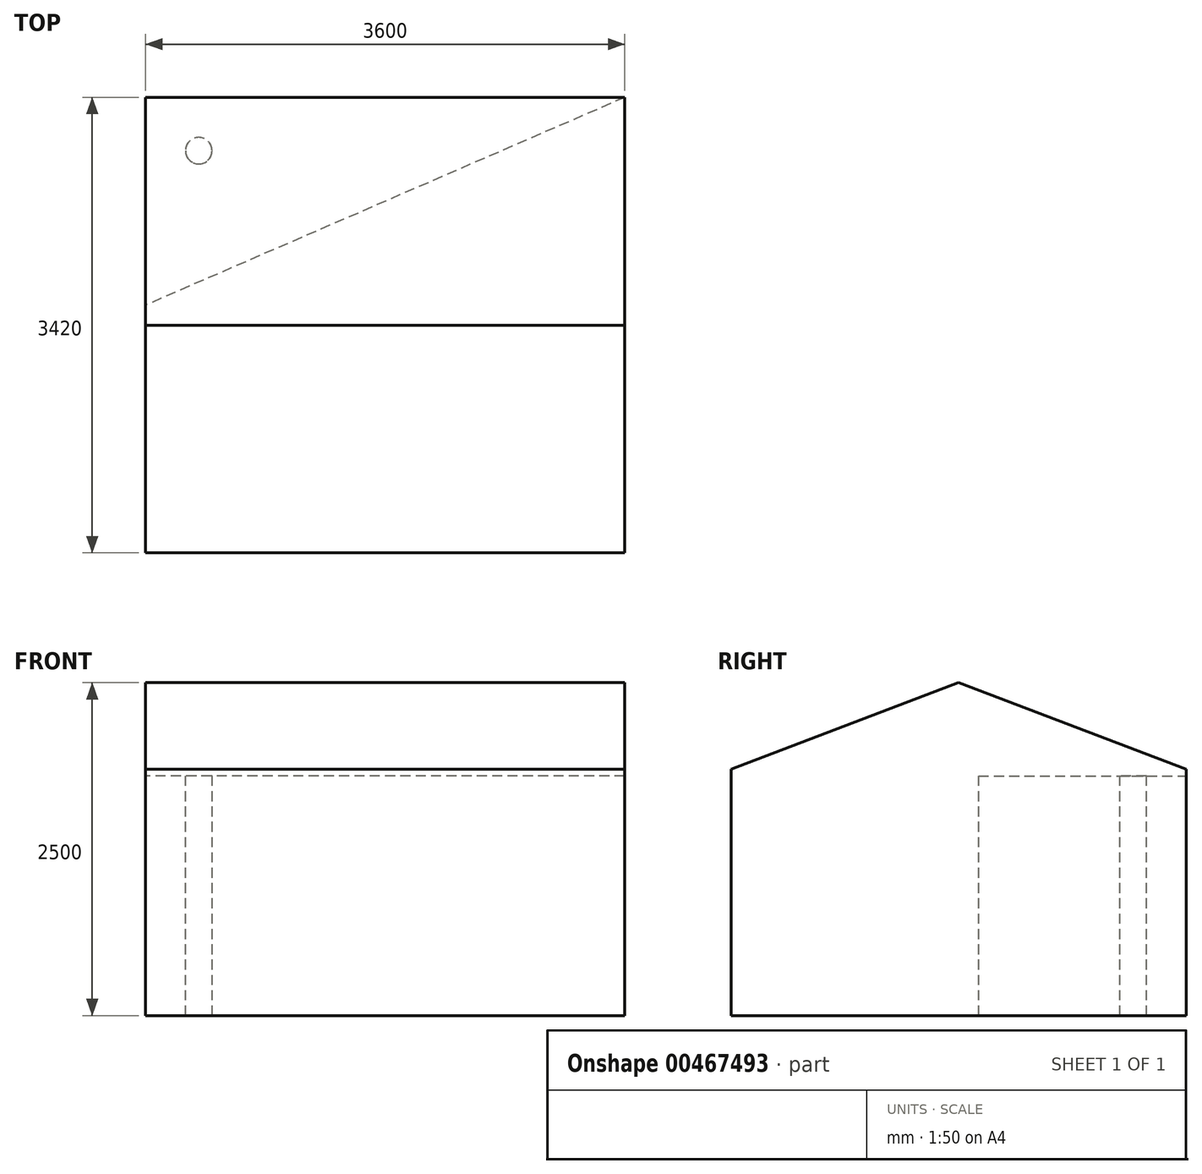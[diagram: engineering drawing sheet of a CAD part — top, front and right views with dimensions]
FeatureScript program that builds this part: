
annotation { "Feature Type Name" : "Feature", "Feature Type Description" : "" }
export const myFeature = defineFeature(function(context is Context, id is Id, definition is map)
    precondition{}
    {
        {
            var Q0;
            Q0=qCreatedBy(makeId("Top.planeOp"),FACE);
            var sketch = newSketch(context, id + "F0", { "sketchPlane" : qUnion([Q0])});
            skLineSegment(sketch, "E0.bottom", {"start": v(-1800, -1710) * mm, "end": v(1800, -1710) * mm});
            skLineSegment(sketch, "E0.left", {"start": v(-1800, -1710) * mm, "end": v(-1800, 150) * mm});
            skLineSegment(sketch, "E0.right", {"start": v(1800, -1710) * mm, "end": v(1800, 150) * mm});
            skPoint(sketch, "E0.middle", {"position": v(0, 0) * mm});
            skPoint(sketch, "E0.top.end.orphan", {"position": v(1800, 1710) * mm});
            skLineSegment(sketch, "E1.right", {"start": v(1800, 1710) * mm, "end": v(1800, 150) * mm});
            skLineSegment(sketch, "E2", {"start": v(1800, 1710) * mm, "end": v(-1800, 150) * mm});
            skPoint(sketch, "E3.orphan", {"position": v(-1800, 1710) * mm});
            skSolve(sketch);
        }
        {
            var Q0;
            Q0=makeQuery(id+"F0.imprint","IMPRINT",FACE,{"disambiguationData":[TD([[makeQuery(id+"F0.imprint","IMPRINT",EDGE,{"derivedFrom":sQuery(id+"F0.wireOp",EDGE,"E0.bottom")}),1.0]])]});
            extrude(context, id + "F1", {"entities" : qUnion([Q0]), "oppositeDirection" : true, "depth" : 1800 * mm});
        }
        {
            var Q0;
            Q0=makeQuery(id+"F1.opExtrude","CAP_FACE",FACE,{"disambiguationData":[OSD([sQuery(id+"F0.wireOp",EDGE,"E0.bottom"),sQuery(id+"F0.wireOp",EDGE,"E0.left"),sQuery(id+"F0.wireOp",EDGE,"E0.right"),sQuery(id+"F0.wireOp",EDGE,"E1.right"),sQuery(id+"F0.wireOp",EDGE,"E2")])],"isStart":true});
            var sketch = newSketch(context, id + "F2", { "sketchPlane" : qUnion([Q0])});
            skLineSegment(sketch, "E4.bottom", {"start": v(-1800, -1710) * mm, "end": v(1800, -1710) * mm});
            skLineSegment(sketch, "E4.top", {"start": v(-1800, 1710) * mm, "end": v(1800, 1710) * mm});
            skLineSegment(sketch, "E4.left", {"start": v(-1800, -1710) * mm, "end": v(-1800, 1710) * mm});
            skLineSegment(sketch, "E4.right", {"start": v(1800, -1710) * mm, "end": v(1800, 1710) * mm});
            skSolve(sketch);
        }
        {
            var Q0;
            Q0 = qSketchRegion(id + "F2", true);
            extrude(context, id + "F3", {"entities" : qUnion([Q0]), "operationType" : NewBodyOperationType.ADD, "depth" : 50 * mm});
        }
        {
            var Q0;
            Q0=makeQuery(id+"F3.boolean.opBoolean","MERGE",FACE,{"derivedFrom":[makeQuery(id+"F1.opExtrude","SWEPT_FACE",FACE,{"disambiguationData":[OSD([sQuery(id+"F0.wireOp",EDGE,"E0.right"),sQuery(id+"F0.wireOp",EDGE,"E1.right")])]}),makeQuery(id+"F3.opExtrude","SWEPT_FACE",FACE,{"disambiguationData":[OSD([sQuery(id+"F2.wireOp",EDGE,"E4.right")])]})]});
            var sketch = newSketch(context, id + "F4", { "sketchPlane" : qUnion([Q0])});
            skLineSegment(sketch, "E5", {"start": v(0, -1800) * mm, "end": v(0, 700) * mm});
            skPoint(sketch, "E5.endSnap0", {"position": v(0, -1800) * mm});
            skLineSegment(sketch, "E6", {"start": v(-1710, 50) * mm, "end": v(0, 700) * mm});
            skLineSegment(sketch, "E7", {"start": v(0, 700) * mm, "end": v(1710, 50) * mm});
            skSolve(sketch);
        }
        {
            var Q0;
            Q0=makeQuery(id+"F3.boolean.opBoolean","MERGE",FACE,{"derivedFrom":[makeQuery(id+"F1.opExtrude","SWEPT_FACE",FACE,{"disambiguationData":[OSD([sQuery(id+"F0.wireOp",EDGE,"E0.left")])]}),makeQuery(id+"F3.opExtrude","SWEPT_FACE",FACE,{"disambiguationData":[OSD([sQuery(id+"F2.wireOp",EDGE,"E4.left")])]})]});
            var sketch = newSketch(context, id + "F5", { "sketchPlane" : qUnion([Q0])});
            skLineSegment(sketch, "E8", {"start": v(0, -1800) * mm, "end": v(0, 700) * mm});
            skLineSegment(sketch, "E9", {"start": v(0, 700) * mm, "end": v(-1710, 50) * mm});
            skLineSegment(sketch, "E10", {"start": v(0, 700) * mm, "end": v(1710, 50) * mm});
            skSolve(sketch);
        }
        {
            var Q0;
            {var subQ0=sQuery(id+"F5.wireOp",EDGE,"E9");Q0=makeQuery(id+"F5.imprint","IMPRINT",FACE,{"disambiguationData":[TD([[makeQuery(id+"F5.imprint","IMPRINT",EDGE,{"derivedFrom":subQ0}),1.0]])]});}
            var Q1;
            {var subQ0=sQuery(id+"F5.wireOp",EDGE,"E10");Q1=makeQuery(id+"F5.imprint","IMPRINT",FACE,{"disambiguationData":[TD([[makeQuery(id+"F5.imprint","IMPRINT",EDGE,{"derivedFrom":subQ0}),-1.0]])]});}
            extrude(context, id + "F6", {"entities" : qUnion([Q0, Q1]), "operationType" : NewBodyOperationType.ADD, "oppositeDirection" : true, "depth" : 3600 * mm});
        }
        {
            var Q0;
            Q0=makeQuery(id+"F3.opExtrude","CAP_FACE",FACE,{"disambiguationData":[OSD([sQuery(id+"F2.wireOp",EDGE,"E4.bottom"),sQuery(id+"F2.wireOp",EDGE,"E4.top"),sQuery(id+"F2.wireOp",EDGE,"E4.left"),sQuery(id+"F2.wireOp",EDGE,"E4.right")])],"isStart":true});
            var sketch = newSketch(context, id + "F7", { "sketchPlane" : qUnion([Q0])});
            skLineSegment(sketch, "E11.bottom", {"start": v(-1800, -1710) * mm, "end": v(-1400, -1710) * mm});
            skLineSegment(sketch, "E11.top", {"start": v(-1800, -1310) * mm, "end": v(-1400, -1310) * mm});
            skLineSegment(sketch, "E11.left", {"start": v(-1800, -1710) * mm, "end": v(-1800, -1310) * mm});
            skLineSegment(sketch, "E11.right", {"start": v(-1400, -1710) * mm, "end": v(-1400, -1310) * mm});
            skCircle(sketch, "E12", {"center": v(-1400, -1310) * mm, "radius": 100 * mm});
            skSolve(sketch);
        }
        {
            var Q0;
            {var subQ0=sQuery(id+"F7.wireOp",EDGE,"E11.right");var subQ1=sQuery(id+"F7.wireOp",EDGE,"E11.top");var subQ2=makeQuery(id+"F7.imprint","INTERSECT",VERTEX,{"derivedFrom":[subQ1,subQ0]});Q0=makeQuery(id+"F7.imprint","IMPRINT",FACE,{"disambiguationData":[TD([[makeQuery(id+"F7.imprint","IMPRINT",EDGE,{"disambiguationData":[TD([[subQ2,1.0]])],"derivedFrom":subQ1}),-1.0]])]});}
            var Q1;
            {var subQ0=sQuery(id+"F7.wireOp",EDGE,"E11.right");var subQ1=sQuery(id+"F7.wireOp",EDGE,"E11.top");var subQ2=makeQuery(id+"F7.imprint","INTERSECT",VERTEX,{"derivedFrom":[subQ1,subQ0]});Q1=makeQuery(id+"F7.imprint","IMPRINT",FACE,{"disambiguationData":[TD([[makeQuery(id+"F7.imprint","IMPRINT",EDGE,{"disambiguationData":[TD([[subQ2,1.0]])],"derivedFrom":subQ1}),1.0]])]});}
            extrude(context, id + "F8", {"entities" : qUnion([Q0, Q1]), "operationType" : NewBodyOperationType.ADD, "depth" : 1800 * mm});
        }
    });
